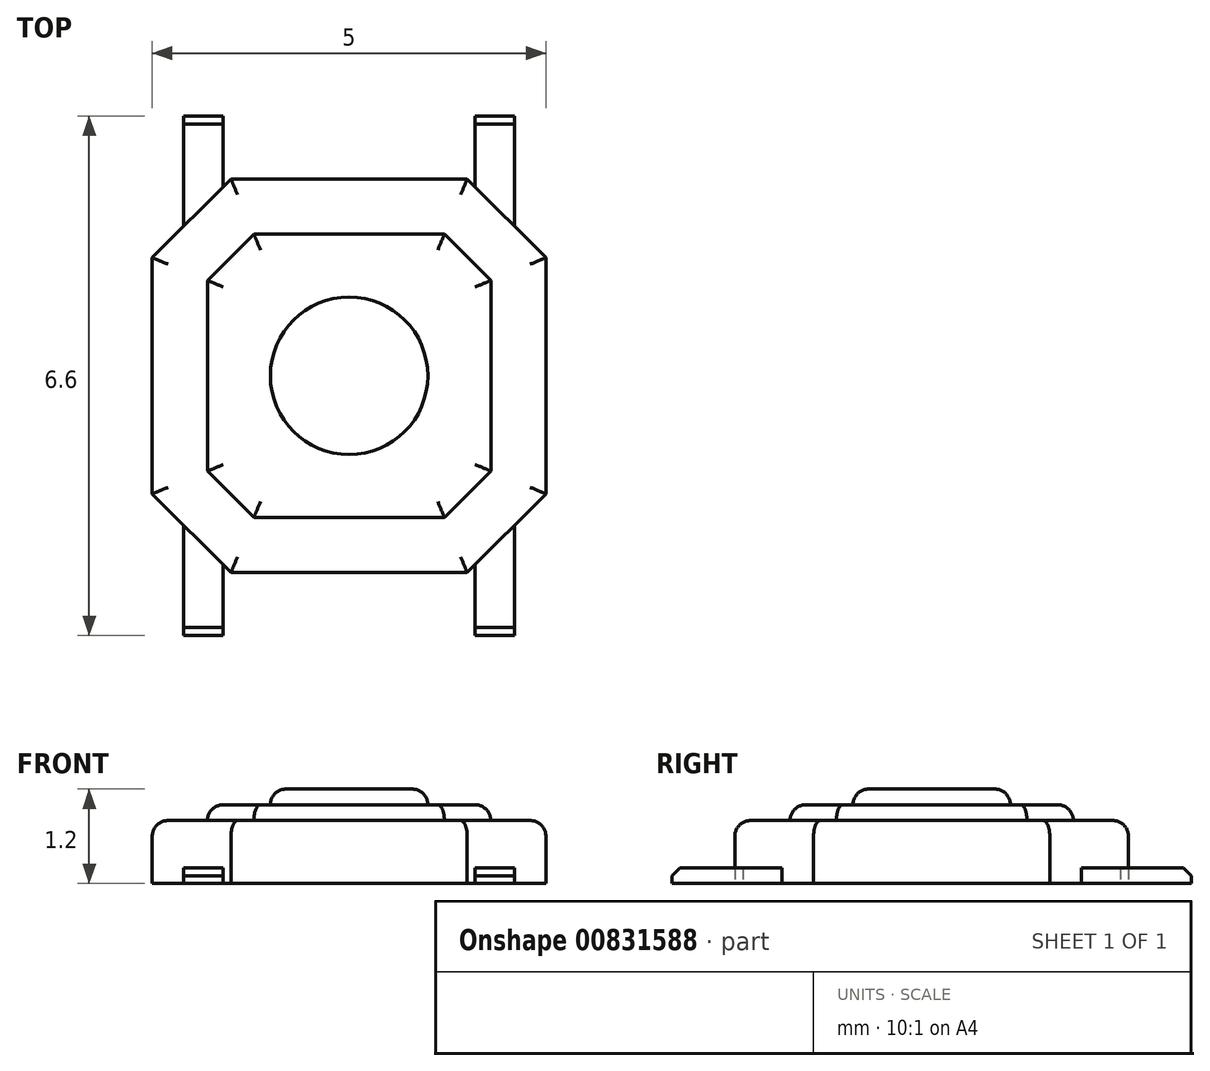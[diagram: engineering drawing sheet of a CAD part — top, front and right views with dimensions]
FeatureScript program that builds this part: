
annotation { "Feature Type Name" : "Feature", "Feature Type Description" : "" }
export const myFeature = defineFeature(function(context is Context, id is Id, definition is map)
    precondition{}
    {
        {
            var Q0;
            Q0=qCreatedBy(makeId("Top.planeOp"),FACE);
            var sketch = newSketch(context, id + "F0", { "sketchPlane" : qUnion([Q0])});
            skLineSegment(sketch, "E0.bottom", {"start": v(-2.5, 2.5) * mm, "end": v(2.5, 2.5) * mm});
            skLineSegment(sketch, "E0.top", {"start": v(-2.5, -2.5) * mm, "end": v(2.5, -2.5) * mm});
            skLineSegment(sketch, "E0.left", {"start": v(-2.5, 2.5) * mm, "end": v(-2.5, -2.5) * mm});
            skLineSegment(sketch, "E0.right", {"start": v(2.5, 2.5) * mm, "end": v(2.5, -2.5) * mm});
            skPoint(sketch, "E0.middle", {"position": v(0, 0) * mm});
            skLineSegment(sketch, "E1.bottom", {"start": v(-2.1, 2.5) * mm, "end": v(-1.6, 2.5) * mm});
            skLineSegment(sketch, "E1.top", {"start": v(-2.1, 3.3) * mm, "end": v(-1.6, 3.3) * mm});
            skLineSegment(sketch, "E1.left", {"start": v(-2.1, 2.5) * mm, "end": v(-2.1, 3.3) * mm});
            skLineSegment(sketch, "E1.right", {"start": v(-1.6, 2.5) * mm, "end": v(-1.6, 3.3) * mm});
            skLineSegment(sketch, "E2.bottom", {"start": v(1.6, 2.5) * mm, "end": v(2.1, 2.5) * mm});
            skLineSegment(sketch, "E2.top", {"start": v(1.6, 3.3) * mm, "end": v(2.1, 3.3) * mm});
            skLineSegment(sketch, "E2.left", {"start": v(1.6, 2.5) * mm, "end": v(1.6, 3.3) * mm});
            skLineSegment(sketch, "E2.right", {"start": v(2.1, 2.5) * mm, "end": v(2.1, 3.3) * mm});
            skLineSegment(sketch, "E3.bottom", {"start": v(-1.6, -2.5) * mm, "end": v(-2.1, -2.5) * mm});
            skLineSegment(sketch, "E3.top", {"start": v(-1.6, -3.3) * mm, "end": v(-2.1, -3.3) * mm});
            skLineSegment(sketch, "E3.left", {"start": v(-1.6, -2.5) * mm, "end": v(-1.6, -3.3) * mm});
            skLineSegment(sketch, "E3.right", {"start": v(-2.1, -2.5) * mm, "end": v(-2.1, -3.3) * mm});
            skLineSegment(sketch, "E4.bottom", {"start": v(2.1, -2.5) * mm, "end": v(1.6, -2.5) * mm});
            skLineSegment(sketch, "E4.top", {"start": v(2.1, -3.3) * mm, "end": v(1.6, -3.3) * mm});
            skLineSegment(sketch, "E4.left", {"start": v(2.1, -2.5) * mm, "end": v(2.1, -3.3) * mm});
            skLineSegment(sketch, "E4.right", {"start": v(1.6, -2.5) * mm, "end": v(1.6, -3.3) * mm});
            skLineSegment(sketch, "E5", {"start": v(-1.5, -2.5) * mm, "end": v(-2.5, -1.5) * mm});
            skLineSegment(sketch, "E6", {"start": v(-2.5, 1.5) * mm, "end": v(-1.5, 2.5) * mm});
            skLineSegment(sketch, "E7", {"start": v(1.5, 2.5) * mm, "end": v(2.5, 1.5) * mm});
            skLineSegment(sketch, "E8", {"start": v(2.5, -1.5) * mm, "end": v(1.5, -2.5) * mm});
            skLineSegment(sketch, "E9", {"start": v(-2.1, -2.5) * mm, "end": v(-2.1, -1.9) * mm});
            skLineSegment(sketch, "E10", {"start": v(-1.6, -2.5) * mm, "end": v(-1.6, -2.4) * mm});
            skLineSegment(sketch, "E11", {"start": v(-2.1, 2.5) * mm, "end": v(-2.1, 1.9) * mm});
            skLineSegment(sketch, "E12", {"start": v(-1.6, 2.5) * mm, "end": v(-1.6, 2.4) * mm});
            skLineSegment(sketch, "E13", {"start": v(1.6, 2.5) * mm, "end": v(1.6, 2.4) * mm});
            skLineSegment(sketch, "E14", {"start": v(2.1, 2.5) * mm, "end": v(2.1, 1.9) * mm});
            skLineSegment(sketch, "E15", {"start": v(1.6, -2.5) * mm, "end": v(1.6, -2.4) * mm});
            skLineSegment(sketch, "E16", {"start": v(2.1, -2.5) * mm, "end": v(2.1, -1.9) * mm});
            skSolve(sketch);
        }
        {
            var Q0;
            {var subQ0=sQuery(id+"F0.wireOp",EDGE,"E6");var subQ1=sQuery(id+"F0.wireOp",EDGE,"E0.bottom");var subQ2=makeQuery(id+"F0.imprint","INTERSECT",VERTEX,{"derivedFrom":[subQ1,subQ0]});Q0=makeQuery(id+"F0.imprint","IMPRINT",FACE,{"disambiguationData":[TD([[makeQuery(id+"F0.imprint","IMPRINT",EDGE,{"disambiguationData":[TD([[subQ2,-1.0]])],"derivedFrom":subQ1}),-1.0]])]});}
            extrude(context, id + "F1", {"entities" : qUnion([Q0]), "depth" : 0.8 * mm, "offsetDistance" : 25 * mm});
        }
        {
            var Q0;
            {var subQ2=sQuery(id+"F0.wireOp",EDGE,"E9");Q0=makeQuery(id+"F0.imprint","IMPRINT",FACE,{"disambiguationData":[TD([[makeQuery(id+"F0.imprint","IMPRINT",EDGE,{"derivedFrom":subQ2}),-1.0]])]});}
            var Q1;
            Q1=makeQuery(id+"F0.imprint","IMPRINT",FACE,{"disambiguationData":[TD([[makeQuery(id+"F0.imprint","IMPRINT",EDGE,{"derivedFrom":sQuery(id+"F0.wireOp",EDGE,"E3.top")}),-1.0]])]});
            var Q2;
            Q2=makeQuery(id+"F0.imprint","IMPRINT",FACE,{"disambiguationData":[TD([[makeQuery(id+"F0.imprint","IMPRINT",EDGE,{"derivedFrom":sQuery(id+"F0.wireOp",EDGE,"E1.top")}),-1.0]])]});
            var Q3;
            {var subQ0=sQuery(id+"F0.wireOp",EDGE,"E11");Q3=makeQuery(id+"F0.imprint","IMPRINT",FACE,{"disambiguationData":[TD([[makeQuery(id+"F0.imprint","IMPRINT",EDGE,{"derivedFrom":subQ0}),1.0]])]});}
            var Q4;
            Q4=makeQuery(id+"F0.imprint","IMPRINT",FACE,{"disambiguationData":[TD([[makeQuery(id+"F0.imprint","IMPRINT",EDGE,{"derivedFrom":sQuery(id+"F0.wireOp",EDGE,"E2.top")}),-1.0]])]});
            var Q5;
            {var subQ0=sQuery(id+"F0.wireOp",EDGE,"E13");Q5=makeQuery(id+"F0.imprint","IMPRINT",FACE,{"disambiguationData":[TD([[makeQuery(id+"F0.imprint","IMPRINT",EDGE,{"derivedFrom":subQ0}),1.0]])]});}
            var Q6;
            {var subQ0=sQuery(id+"F0.wireOp",EDGE,"E15");Q6=makeQuery(id+"F0.imprint","IMPRINT",FACE,{"disambiguationData":[TD([[makeQuery(id+"F0.imprint","IMPRINT",EDGE,{"derivedFrom":subQ0}),-1.0]])]});}
            var Q7;
            Q7=makeQuery(id+"F0.imprint","IMPRINT",FACE,{"disambiguationData":[TD([[makeQuery(id+"F0.imprint","IMPRINT",EDGE,{"derivedFrom":sQuery(id+"F0.wireOp",EDGE,"E4.top")}),-1.0]])]});
            extrude(context, id + "F2", {"entities" : qUnion([Q0, Q1, Q2, Q3, Q4, Q5, Q6, Q7]), "depth" : 0.2 * mm, "offsetDistance" : 25 * mm});
        }
        {
            var Q0;
            Q0=makeQuery(id+"F1.opExtrude","CAP_FACE",FACE,{"disambiguationData":[OSD([sQuery(id+"F0.wireOp",EDGE,"E0.bottom"),sQuery(id+"F0.wireOp",EDGE,"E0.top"),sQuery(id+"F0.wireOp",EDGE,"E0.left"),sQuery(id+"F0.wireOp",EDGE,"E0.right"),sQuery(id+"F0.wireOp",EDGE,"E5"),sQuery(id+"F0.wireOp",EDGE,"E6"),sQuery(id+"F0.wireOp",EDGE,"E7"),sQuery(id+"F0.wireOp",EDGE,"E8")])],"isStart":false});
            fillet(context, id + "F3", {"entities" : qUnion([Q0]), "radius" : 0.2 * mm, "tangentPropagation" : true, "allowEdgeOverflow" : false});
        }
        {
            var Q0;
            Q0=makeQuery(id+"F1.opExtrude","CAP_FACE",FACE,{"disambiguationData":[OSD([sQuery(id+"F0.wireOp",EDGE,"E0.bottom"),sQuery(id+"F0.wireOp",EDGE,"E0.top"),sQuery(id+"F0.wireOp",EDGE,"E0.left"),sQuery(id+"F0.wireOp",EDGE,"E0.right"),sQuery(id+"F0.wireOp",EDGE,"E5"),sQuery(id+"F0.wireOp",EDGE,"E6"),sQuery(id+"F0.wireOp",EDGE,"E7"),sQuery(id+"F0.wireOp",EDGE,"E8")])],"isStart":false});
            var sketch = newSketch(context, id + "F4", { "sketchPlane" : qUnion([Q0])});
            skLineSegment(sketch, "E17.0", {"start": v(-1.21, 1.8) * mm, "end": v(-1.8, 1.21) * mm});
            skLineSegment(sketch, "E17.1", {"start": v(1.21, 1.8) * mm, "end": v(-1.21, 1.8) * mm});
            skLineSegment(sketch, "E17.2", {"start": v(-1.8, 1.21) * mm, "end": v(-1.8, -1.21) * mm});
            skLineSegment(sketch, "E17.3", {"start": v(1.8, 1.21) * mm, "end": v(1.21, 1.8) * mm});
            skLineSegment(sketch, "E17.4", {"start": v(-1.8, -1.21) * mm, "end": v(-1.21, -1.8) * mm});
            skLineSegment(sketch, "E17.5", {"start": v(-1.21, -1.8) * mm, "end": v(1.21, -1.8) * mm});
            skLineSegment(sketch, "E17.6", {"start": v(1.21, -1.8) * mm, "end": v(1.8, -1.21) * mm});
            skLineSegment(sketch, "E17.7", {"start": v(1.8, -1.21) * mm, "end": v(1.8, 1.21) * mm});
            skSolve(sketch);
        }
        {
            var Q0;
            Q0 = qSketchRegion(id + "F4", true);
            extrude(context, id + "F5", {"entities" : qUnion([Q0]), "operationType" : NewBodyOperationType.ADD, "depth" : 0.2 * mm, "offsetDistance" : 25 * mm});
        }
        {
            var Q0;
            Q0=makeQuery(id+"F5.opExtrude","CAP_FACE",FACE,{"disambiguationData":[OSD([sQuery(id+"F4.wireOp",EDGE,"E17.0"),sQuery(id+"F4.wireOp",EDGE,"E17.1"),sQuery(id+"F4.wireOp",EDGE,"E17.2"),sQuery(id+"F4.wireOp",EDGE,"E17.3"),sQuery(id+"F4.wireOp",EDGE,"E17.4"),sQuery(id+"F4.wireOp",EDGE,"E17.5"),sQuery(id+"F4.wireOp",EDGE,"E17.6"),sQuery(id+"F4.wireOp",EDGE,"E17.7")])],"isStart":false});
            fillet(context, id + "F6", {"entities" : qUnion([Q0]), "radius" : 0.2 * mm, "tangentPropagation" : true, "allowEdgeOverflow" : false});
        }
        {
            var Q0;
            Q0=makeQuery(id+"F5.opExtrude","CAP_FACE",FACE,{"disambiguationData":[OSD([sQuery(id+"F4.wireOp",EDGE,"E17.0"),sQuery(id+"F4.wireOp",EDGE,"E17.1"),sQuery(id+"F4.wireOp",EDGE,"E17.2"),sQuery(id+"F4.wireOp",EDGE,"E17.3"),sQuery(id+"F4.wireOp",EDGE,"E17.4"),sQuery(id+"F4.wireOp",EDGE,"E17.5"),sQuery(id+"F4.wireOp",EDGE,"E17.6"),sQuery(id+"F4.wireOp",EDGE,"E17.7")])],"isStart":false});
            var sketch = newSketch(context, id + "F7", { "sketchPlane" : qUnion([Q0])});
            skCircle(sketch, "E18", {"center": v(0, 0) * mm, "radius": 1 * mm});
            skSolve(sketch);
        }
        {
            var Q0;
            Q0 = qSketchRegion(id + "F7", true);
            extrude(context, id + "F8", {"entities" : qUnion([Q0]), "depth" : 0.2 * mm, "offsetDistance" : 25 * mm});
        }
        {
            var Q0;
            Q0=makeQuery(id+"F8.opExtrude","CAP_FACE",FACE,{"disambiguationData":[OSD([sQuery(id+"F7.wireOp",EDGE,"E18")])],"isStart":false});
            fillet(context, id + "F9", {"entities" : qUnion([Q0]), "radius" : 0.2 * mm, "tangentPropagation" : true, "allowEdgeOverflow" : false});
        }
        {
            var Q0;
            Q0=makeQuery(id+"F2.opExtrude","CAP_EDGE",EDGE,{"disambiguationData":[OSD([sQuery(id+"F0.wireOp",EDGE,"E1.top")])],"isStart":false});
            var Q1;
            Q1=makeQuery(id+"F2.opExtrude","CAP_EDGE",EDGE,{"disambiguationData":[OSD([sQuery(id+"F0.wireOp",EDGE,"E2.top")])],"isStart":false});
            var Q2;
            Q2=makeQuery(id+"F2.opExtrude","CAP_EDGE",EDGE,{"disambiguationData":[OSD([sQuery(id+"F0.wireOp",EDGE,"E4.top")])],"isStart":false});
            var Q3;
            Q3=makeQuery(id+"F2.opExtrude","CAP_EDGE",EDGE,{"disambiguationData":[OSD([sQuery(id+"F0.wireOp",EDGE,"E3.top")])],"isStart":false});
            chamfer(context, id + "F10", {"entities" : qUnion([Q0, Q1, Q2, Q3]), "width" : 0.1 * mm, "tangentPropagation" : true});
        }
    });
